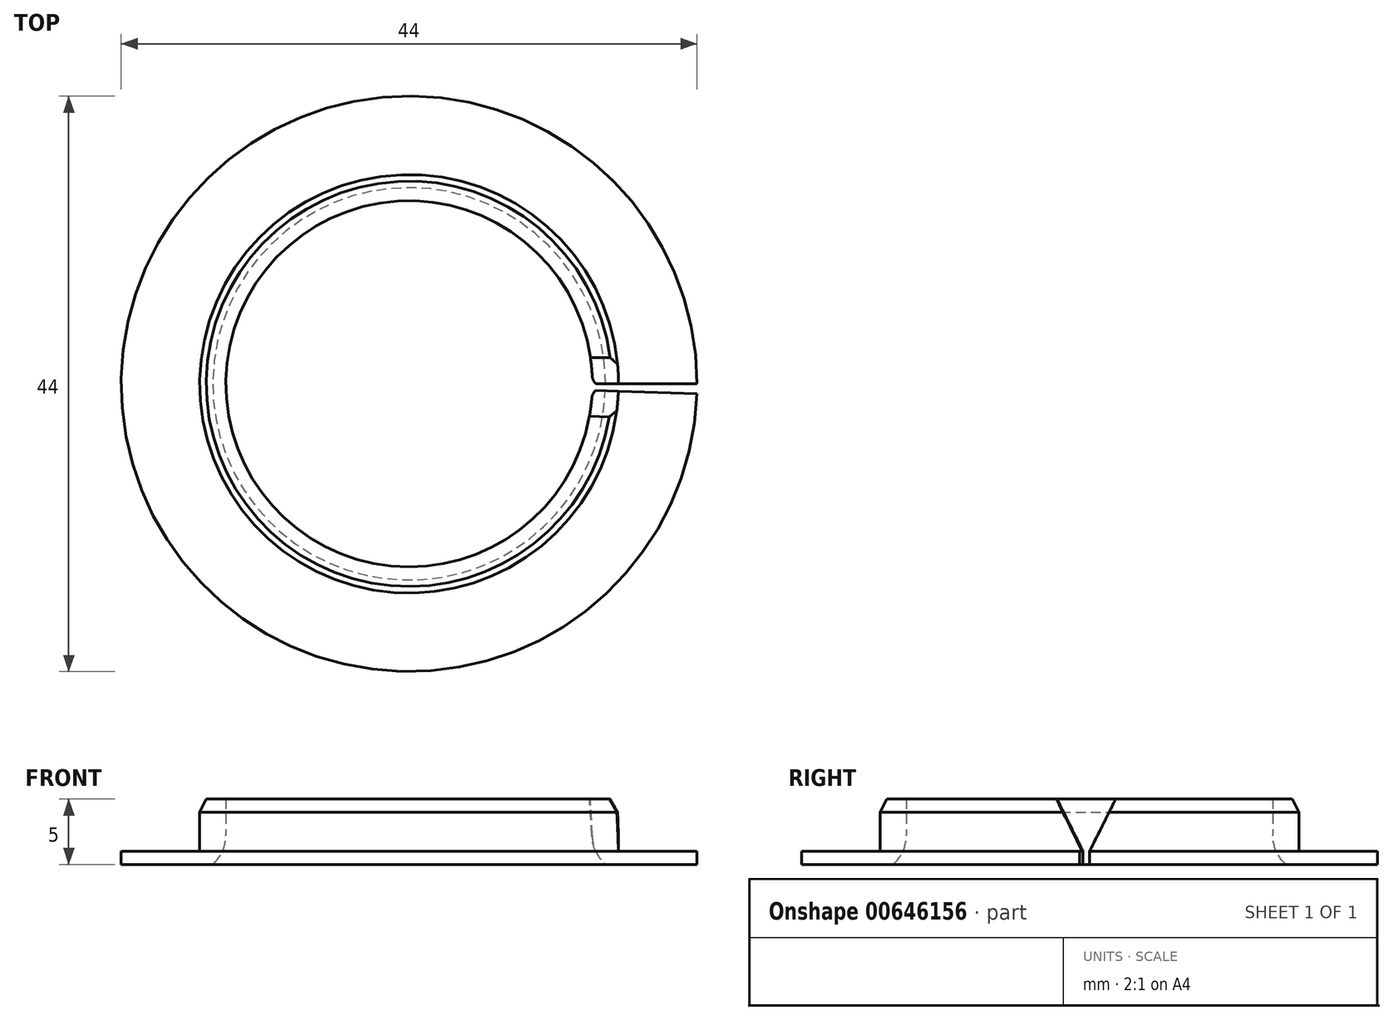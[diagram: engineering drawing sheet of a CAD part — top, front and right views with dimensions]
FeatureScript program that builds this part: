
annotation { "Feature Type Name" : "Feature", "Feature Type Description" : "" }
export const myFeature = defineFeature(function(context is Context, id is Id, definition is map)
    precondition{}
    {
        {
            var Q0;
            Q0=qCreatedBy(makeId("Front.planeOp"),FACE);
            var sketch = newSketch(context, id + "F0", { "sketchPlane" : qUnion([Q0])});
            skLineSegment(sketch, "E0", {"start": v(0, -18.85) * mm, "end": v(0, 18.75) * mm, "construction": true});
            skLineSegment(sketch, "E1", {"start": v(0, 18.75) * mm, "end": v(0, -18.85) * mm, "construction": true});
            skLineSegment(sketch, "E2", {"start": v(22, 0) * mm, "end": v(14, 0) * mm});
            skLineSegment(sketch, "E3", {"start": v(14, 0) * mm, "end": v(14, 5) * mm});
            skLineSegment(sketch, "E4", {"start": v(14, 5) * mm, "end": v(16, 5) * mm});
            skLineSegment(sketch, "E5", {"start": v(16, 5) * mm, "end": v(16, 1) * mm});
            skLineSegment(sketch, "E6", {"start": v(16, 1) * mm, "end": v(22, 1) * mm});
            skLineSegment(sketch, "E7", {"start": v(22, 1) * mm, "end": v(22, 0) * mm});
            skSolve(sketch);
        }
        {
            var Q0;
            Q0 = qSketchRegion(id + "F0", true);
            var Q1;
            Q1=sQuery(id+"F0.wireOp",EDGE,"E0");
            revolve(context, id + "F1", {"entities" : qUnion([Q0]), "axis" : qUnion([Q1]), "revolveType" : RevolveType.ONE_DIRECTION, "angle" : 358 * degree});
        }
        {
            var Q0;
            Q0=makeQuery(id+"F1.opRevolve","CAP_EDGE",EDGE,{"disambiguationData":[OSD([sQuery(id+"F0.wireOp",EDGE,"E4")])],"isStart":false});
            var Q1;
            Q1=makeQuery(id+"F1.opRevolve","CAP_EDGE",EDGE,{"disambiguationData":[OSD([sQuery(id+"F0.wireOp",EDGE,"E4")])],"isStart":true});
            chamfer(context, id + "F2", {"entities" : qUnion([Q0, Q1]), "chamferType" : ChamferType.TWO_OFFSETS, "width1" : 4 * mm, "oppositeDirection" : false, "width2" : 2 * mm, "tangentPropagation" : true});
        }
        {
            var Q0;
            Q0=makeQuery(id+"F1.opRevolve","SWEPT_EDGE",EDGE,{"disambiguationData":[OSD([sQuery(id+"F0.wireOp",EDGE,"E2"),sQuery(id+"F0.wireOp",EDGE,"E3")])]});
            chamfer(context, id + "F3", {"entities" : qUnion([Q0]), "width" : 1 * mm, "tangentPropagation" : true});
        }
        {
            var Q0;
            {var subQ0=sQuery(id+"F0.wireOp",EDGE,"E3");Q0=makeQuery(id+"F3.opChamfer","BLEND_EDGE",EDGE,{"blendedFrom":[makeQuery(id+"F1.opRevolve","SWEPT_EDGE",EDGE,{"disambiguationData":[OSD([sQuery(id+"F0.wireOp",EDGE,"E2"),subQ0])]}),makeQuery(id+"F1.opRevolve","SWEPT_FACE",FACE,{"disambiguationData":[OSD([subQ0])]})],"blendedInto":[makeQuery(id+"F1.opRevolve","SWEPT_FACE",FACE,{"disambiguationData":[OSD([subQ0])]})]});}
            fillet(context, id + "F4", {"entities" : qUnion([Q0]), "radius" : 3 * mm, "tangentPropagation" : true, "allowEdgeOverflow" : false});
        }
        {
            var Q0;
            Q0=makeQuery(id+"F1.opRevolve","SWEPT_EDGE",EDGE,{"disambiguationData":[OSD([sQuery(id+"F0.wireOp",EDGE,"E4"),sQuery(id+"F0.wireOp",EDGE,"E5")])]});
            chamfer(context, id + "F5", {"entities" : qUnion([Q0]), "chamferType" : ChamferType.TWO_OFFSETS, "width1" : 1 * mm, "oppositeDirection" : false, "width2" : 0.5 * mm, "tangentPropagation" : true});
        }
    });
